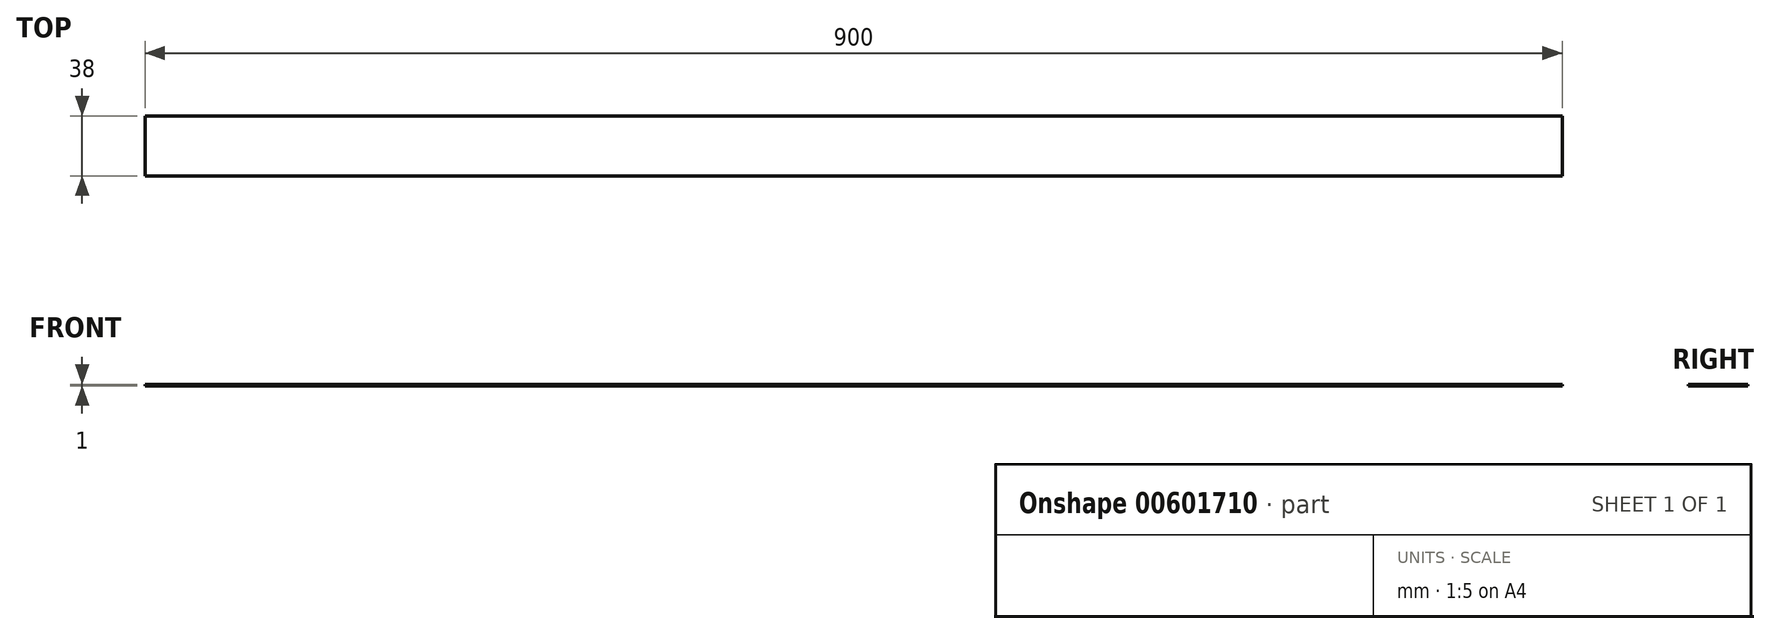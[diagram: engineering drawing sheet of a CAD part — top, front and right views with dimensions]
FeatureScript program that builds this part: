
annotation { "Feature Type Name" : "Feature", "Feature Type Description" : "" }
export const myFeature = defineFeature(function(context is Context, id is Id, definition is map)
    precondition{}
    {
        {
            var Q0;
            Q0=qCreatedBy(makeId("Top.planeOp"),FACE);
            var sketch = newSketch(context, id + "F0", { "sketchPlane" : qUnion([Q0])});
            skLineSegment(sketch, "E0.bottom", {"start": v(-310.9, 19.03) * mm, "end": v(589.1, 19.03) * mm});
            skLineSegment(sketch, "E0.top", {"start": v(-310.9, -18.97) * mm, "end": v(589.1, -18.97) * mm});
            skLineSegment(sketch, "E0.left", {"start": v(-310.9, 19.03) * mm, "end": v(-310.9, -18.97) * mm});
            skLineSegment(sketch, "E0.right", {"start": v(589.1, 19.03) * mm, "end": v(589.1, -18.97) * mm});
            skLineSegment(sketch, "E1", {"start": v(-150.9, 63.12) * mm, "end": v(-150.9, -63.14) * mm, "construction": true});
            skLineSegment(sketch, "E2", {"start": v(-243.37, 0) * mm, "end": v(-101.27, 0) * mm, "construction": true});
            skPoint(sketch, "E3", {"position": v(-150.9, 0) * mm});
            skSolve(sketch);
        }
        {
            var Q0;
            Q0=makeQuery(id+"F0.imprint","IMPRINT",FACE,{"disambiguationData":[TD([[makeQuery(id+"F0.imprint","IMPRINT",EDGE,{"derivedFrom":sQuery(id+"F0.wireOp",EDGE,"E0.bottom")}),-1.0]])]});
            extrude(context, id + "F1", {"entities" : qUnion([Q0]), "depth" : 1 * mm, "offsetDistance" : 25 * mm});
        }
    });
